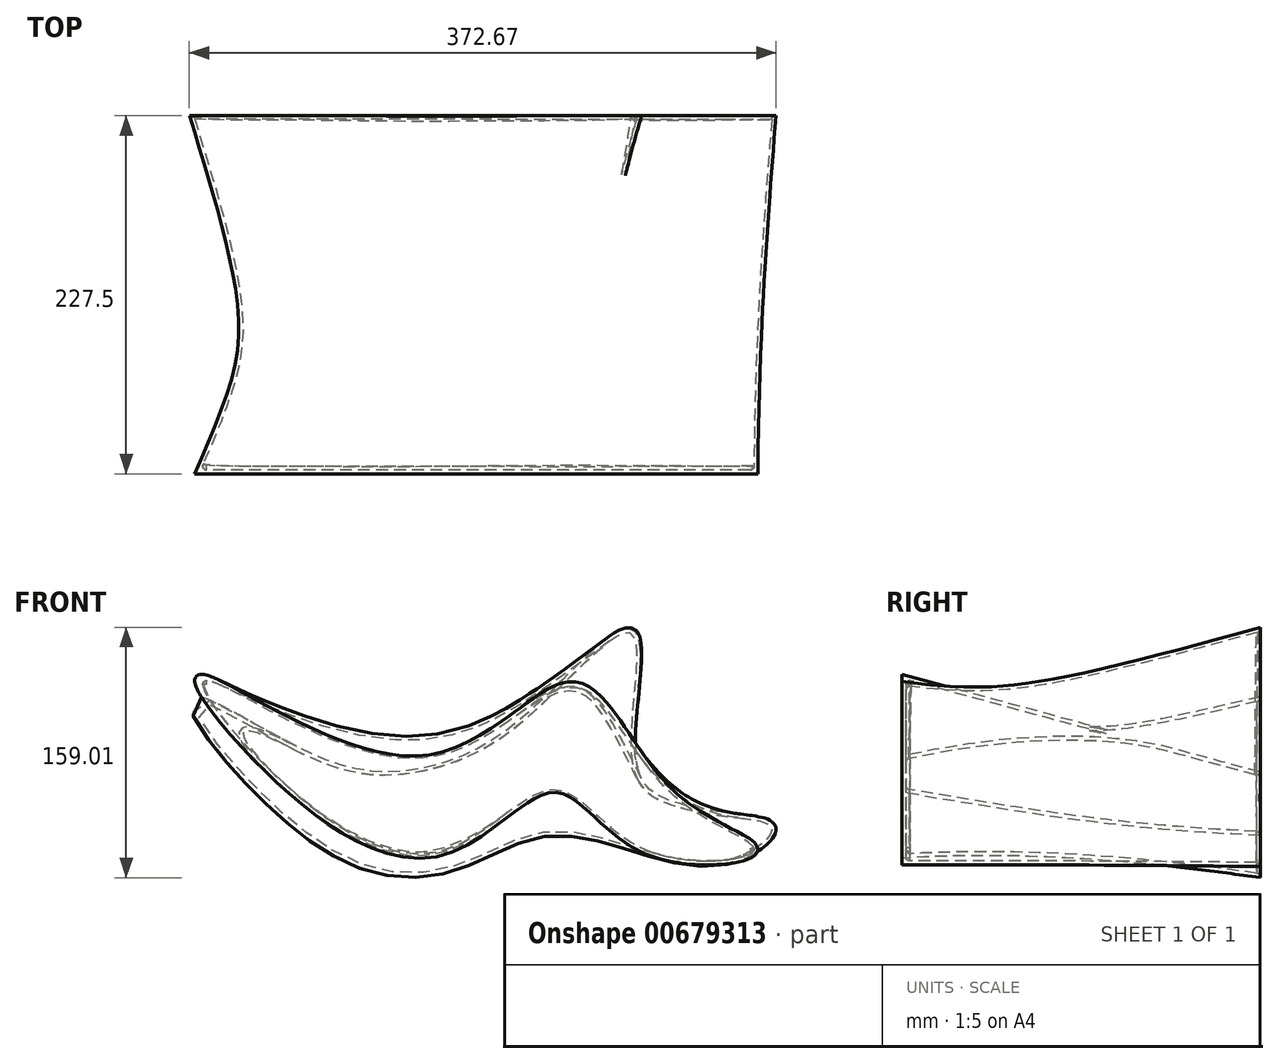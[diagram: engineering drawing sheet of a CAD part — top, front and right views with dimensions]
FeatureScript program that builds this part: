
annotation { "Feature Type Name" : "Feature", "Feature Type Description" : "" }
export const myFeature = defineFeature(function(context is Context, id is Id, definition is map)
    precondition{}
    {
        {
            var Q0;
            Q0=qCreatedBy(makeId("Front.planeOp"),FACE);
            cPlane(context, id + "F0", {"entities" : qUnion([Q0]), "cplaneType" : CPlaneType.OFFSET, "offset" : 450 * mm, "width" : 150 * mm, "height" : 150 * mm});
        }
        {
            var Q0;
            Q0=qCreatedBy(id+"F0.planeOp",FACE);
            var sketch = newSketch(context, id + "F1", { "sketchPlane" : qUnion([Q0])});
            skFitSpline(sketch, "E0", {"points": [v(0, 0) * mm, v(-67.83, 0) * mm, v(-126.8, 38.96) * mm, v(-196.28, 0) * mm, v(-301.57, 45.27) * mm, v(-350, 108.44) * mm, v(-213.13, 57.9) * mm, v(-114.16, 104.23) * mm, v(-50.99, 34.74) * mm, v(0, 0) * mm]});
            skSolve(sketch);
        }
        {
            var Q0;
            Q0=qCreatedBy(id+"F0.planeOp",FACE);
            cPlane(context, id + "F2", {"entities" : qUnion([Q0]), "cplaneType" : CPlaneType.OFFSET, "offset" : 225 * mm, "oppositeDirection" : true, "width" : 150 * mm, "height" : 150 * mm});
        }
        {
            var Q0;
            Q0=qCreatedBy(id+"F2.planeOp",FACE);
            var sketch = newSketch(context, id + "F3", { "sketchPlane" : qUnion([Q0])});
            skFitSpline(sketch, "E1", {"points": [v(-355.43, 94.27) * mm, v(-276.83, 56.86) * mm, v(-207.42, 50.1) * mm, v(-142.8, 84.49) * mm, v(-76.99, 138.12) * mm, v(-76.99, 55.22) * mm, v(-53.06, 28.84) * mm, v(-11.18, 20.77) * mm, v(11.56, 13.89) * mm, v(-18.25, -6.58) * mm, v(-93, 6.77) * mm, v(-141.04, 9.88) * mm, v(-190.87, -10.58) * mm, v(-275.4, 4.55) * mm, v(-355.43, 94.27) * mm]});
            skSolve(sketch);
        }
        {
            var Q0;
            Q0=makeQuery(id+"F1.imprint","IMPRINT",FACE,{"disambiguationData":[TD([[makeQuery(id+"F1.imprint","IMPRINT",EDGE,{"derivedFrom":sQuery(id+"F1.wireOp",EDGE,"E0")}),-1.0]])]});
            var Q1;
            Q1=makeQuery(id+"F3.imprint","IMPRINT",FACE,{"disambiguationData":[TD([[makeQuery(id+"F3.imprint","IMPRINT",EDGE,{"derivedFrom":sQuery(id+"F3.wireOp",EDGE,"E1")}),-1.0]])]});
            loft(context, id + "F4", {"sheetProfilesArray" : [{ "sheetProfileEntities" : qUnion([Q0]) }, { "sheetProfileEntities" : qUnion([Q1]) }]});
        }
        {
            var Q0;
            Q0=makeQuery(id+"F4.opLoft","CAP_FACE",FACE,{"disambiguationData":[OSD([makeQuery(id+"F3.imprint","IMPRINT",FACE,{"disambiguationData":[TD([[makeQuery(id+"F3.imprint","IMPRINT",EDGE,{"derivedFrom":sQuery(id+"F3.wireOp",EDGE,"E1")}),-1.0]])]})])],"isStart":true});
            shell(context, id + "F5", {"entities" : qUnion([Q0]), "thickness" : 2.5 * mm, "oppositeDirection" : true});
        }
        {
            var Q0;
            Q0=makeQuery(id+"F5.opShell","OFFSET_EDGE",EDGE,{"disambiguationData":[OSD([sQuery(id+"F1.wireOp",EDGE,"E0")])]});
            var Q1;
            Q1=makeQuery(id+"F5.opShell","OFFSET_EDGE",EDGE,{"disambiguationData":[OSD([sQuery(id+"F1.wireOp",EDGE,"E0"),sQuery(id+"F3.wireOp",EDGE,"E1")])]});
            fillet(context, id + "F6", {"entities" : qUnion([Q0, Q1]), "radius" : 2.5 * mm, "tangentPropagation" : true, "allowEdgeOverflow" : false});
        }
        {
            var Q0;
            Q0=qCreatedBy(id+"F0.planeOp",FACE);
            var sketch = newSketch(context, id + "F7", { "sketchPlane" : qUnion([Q0])});
            skLineSegment(sketch, "E2", {"start": v(-170, 43.41) * mm, "end": v(0, 43.41) * mm, "construction": true});
            skCircle(sketch, "E3", {"center": v(-170, 43.41) * mm, "radius": 3.88 * mm});
            skSolve(sketch);
        }
        {
            var Q0;
            Q0=qCreatedBy(makeId("Right.planeOp"),FACE);
            cPlane(context, id + "F8", {"entities" : qUnion([Q0]), "cplaneType" : CPlaneType.OFFSET, "offset" : 170 * mm, "oppositeDirection" : true, "width" : 150 * mm, "height" : 150 * mm});
        }
        {
            var Q0;
            Q0=qCreatedBy(id+"F8.planeOp",FACE);
            var sketch = newSketch(context, id + "F9", { "sketchPlane" : qUnion([Q0])});
            skFitSpline(sketch, "E4", {"points": [v(-450.02, 43.18) * mm, v(-487.65, 47.37) * mm, v(-560.64, 92.75) * mm, v(-676.05, 89.71) * mm, v(-771.83, 101.04) * mm], "startDerivative": vector(-209.48, -28.21) * mm, "endDerivative": vector(-334.85, 72.2) * mm});
            skSolve(sketch);
        }
    });
